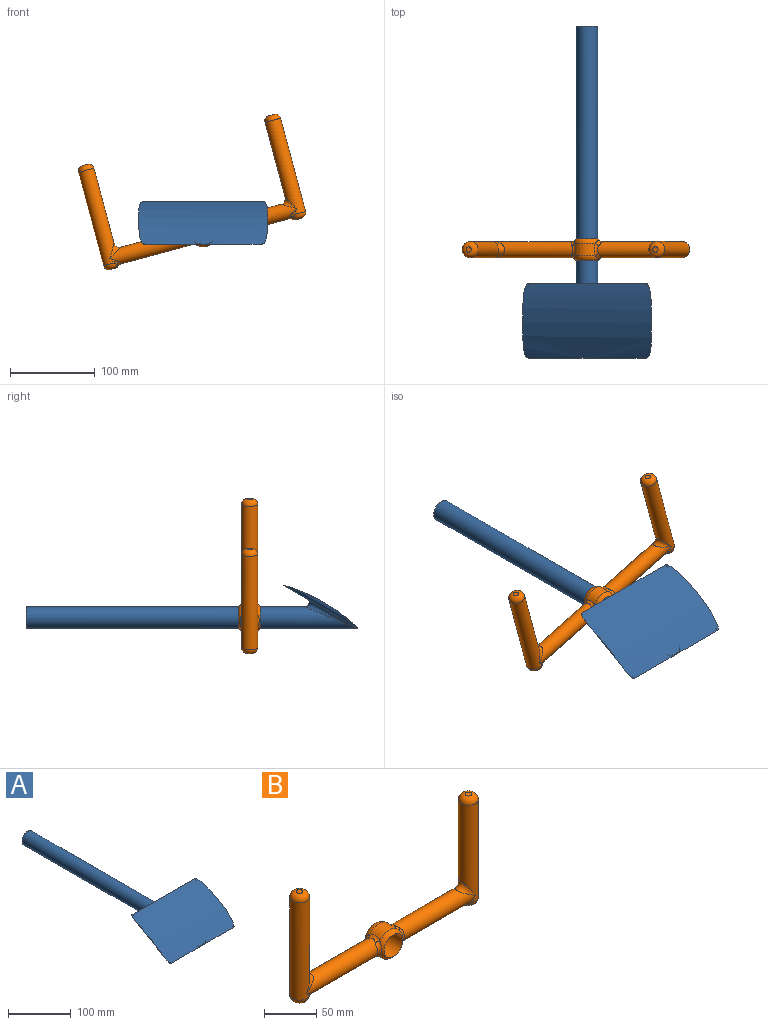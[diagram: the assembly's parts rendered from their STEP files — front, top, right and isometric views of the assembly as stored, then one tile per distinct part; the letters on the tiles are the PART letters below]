
ASSEMBLY  parts=2 mates=1
PART A: 9 faces, bbox 152.4x396x56.3 mm
  f0: plane 139.7x87.99mm, normal (0,0.5,-0.87), area 12216.1mm2, adj f1,f5,f7,f8
  f1: cylinder r=206.38mm len=152.4mm, axis (-1,0,0), area 15479.9mm2, adj f0,f4,f6,f7,f8
  f2: cylinder r=12.7mm len=392.79mm, axis (0,1,0), area 28780.5mm2, adj f3,f4,f5,f6
  f3: plane 25.4x25.4mm, normal (0,1,0), area 506.7mm2, adj f2
  f4: bspline ~5.5x2.84mm, area 4.2mm2, adj f1,f2,f5
  f5: bspline ~62.9x35.56mm, area 1186.2mm2, adj f0,f2,f4,f6
  f6: bspline ~5.5x2.84mm, area 4.2mm2, adj f1,f2,f5
  f7: cylinder r=6.35mm len=91.16mm, axis (0,0.87,0.5), area 506.7mm2, adj f0,f1
  f8: cylinder r=6.35mm len=91.16mm, axis (0,-0.87,-0.5), area 506.7mm2, adj f0,f1
PART B: 39 faces, bbox 247.7x27.1x131.5 mm
  f0: cylinder r=15.88mm len=25.25mm, axis (0,1,0), area 383.7mm2, adj f29,f30,f32,f36
  f1: cylinder r=9.53mm len=97.64mm, axis (-1,0,0), area 5318mm2, adj f20,f21,f22,f23,f24,f26,f31,f32
  f2: cylinder r=12.7mm len=25.4mm, axis (0,1,0), area 2026.8mm2, adj f29,f30
  f3: cylinder r=15.88mm len=25.25mm, axis (0,1,0), area 383.7mm2, adj f29,f30,f33,f37
  f4: cylinder r=9.53mm len=97.64mm, axis (-1,0,0), area 5318mm2, adj f15,f16,f17,f18,f19,f25,f35,f36
  f5: cylinder r=9.53mm len=114.3mm, axis (0,0,-1), area 6373.2mm2, adj f13,f20,f21,f26,f28
  f6: plane 6.35x6.35mm, normal (0,0,1), area 31.7mm2, adj f28
  f7: plane 7.2x6.35mm, normal (0,0,-1), area 33.6mm2, adj f13,f14
  f8: cylinder r=9.53mm len=114.3mm, axis (0,0,-1), area 6437.9mm2, adj f11,f15,f17,f25,f27
  f9: plane 6.35x6.35mm, normal (0,0,1), area 31.7mm2, adj f27
  f10: plane 7.2x6.35mm, normal (0,0,-1), area 33.6mm2, adj f11,f12
  f11: torus R=3.17mm, axis (0,0,1), area 323.4mm2, adj f8,f10,f12,f16,f19
  f12: bspline ~15.22x7.81mm, area 62.1mm2, adj f10,f11,f18
  f13: torus R=3.17mm, axis (0,0,1), area 323.4mm2, adj f5,f7,f14,f22,f23
  f14: bspline ~15.45x7.8mm, area 62.1mm2, adj f7,f13,f24
  f15: bspline ~7.94x7.94mm, area 13.1mm2, adj f4,f8,f16
  f16: bspline ~7.25x6.13mm, area 18mm2, adj f4,f11,f15,f18
  f17: bspline ~7.94x7.94mm, area 8.7mm2, adj f4,f8,f19
  f18: bspline ~14.99x7.2mm, area 66.3mm2, adj f4,f12,f16,f19
  f19: bspline ~7.5x6.4mm, area 18mm2, adj f4,f11,f17,f18
  f20: bspline ~7.94x7.94mm, area 8.7mm2, adj f1,f5,f22
  f21: bspline ~7.94x7.94mm, area 8.7mm2, adj f1,f5,f23
  f22: bspline ~7.5x6.4mm, area 18mm2, adj f1,f13,f20,f24
  f23: bspline ~7.25x6.13mm, area 18mm2, adj f1,f13,f21,f24
  f24: bspline ~14.38x6.87mm, area 66.3mm2, adj f1,f14,f22,f23
  f25: bspline ~19.05x15.88mm, area 149.4mm2, adj f4,f8
  f26: bspline ~19.05x15.88mm, area 216.1mm2, adj f1,f5
  f27: torus R=3.17mm, axis (0,0,1), area 452.3mm2, adj f8,f9
  f28: torus R=3.17mm, axis (0,0,1), area 452.3mm2, adj f5,f6
  f29: torus R=9.53mm, axis (0,1,0), area 491.6mm2, adj f0,f2,f3,f31,f38
  f30: torus R=9.53mm, axis (0,-1,0), area 491.6mm2, adj f0,f2,f3,f34,f35
  f31: bspline ~20.39x8.21mm, area 98.4mm2, adj f1,f29,f32,f33
  f32: bspline ~17.33x5.97mm, area 55.7mm2, adj f0,f1,f31,f34
  f33: bspline ~17.33x5.97mm, area 55.7mm2, adj f1,f3,f31,f34
  f34: bspline ~21.01x8.21mm, area 98.4mm2, adj f1,f30,f32,f33
  f35: bspline ~20.39x8.21mm, area 98.4mm2, adj f4,f30,f36,f37
  f36: bspline ~17.33x5.97mm, area 55.7mm2, adj f0,f4,f35,f38
  f37: bspline ~17.33x5.97mm, area 55.7mm2, adj f3,f4,f35,f38
  f38: bspline ~21.01x8.21mm, area 98.4mm2, adj f4,f29,f36,f37
PLACE A t=(1.37,-310.42,-6.08)mm fixed
PLACE B rot(axis=(0,-1,0),15deg) t=(4.66,-257.58,-5.65)mm
MATE cylindrical A.f2 <-> B.f0  axis (0,1,0) through (1.37,-5.62,6.62)mm
